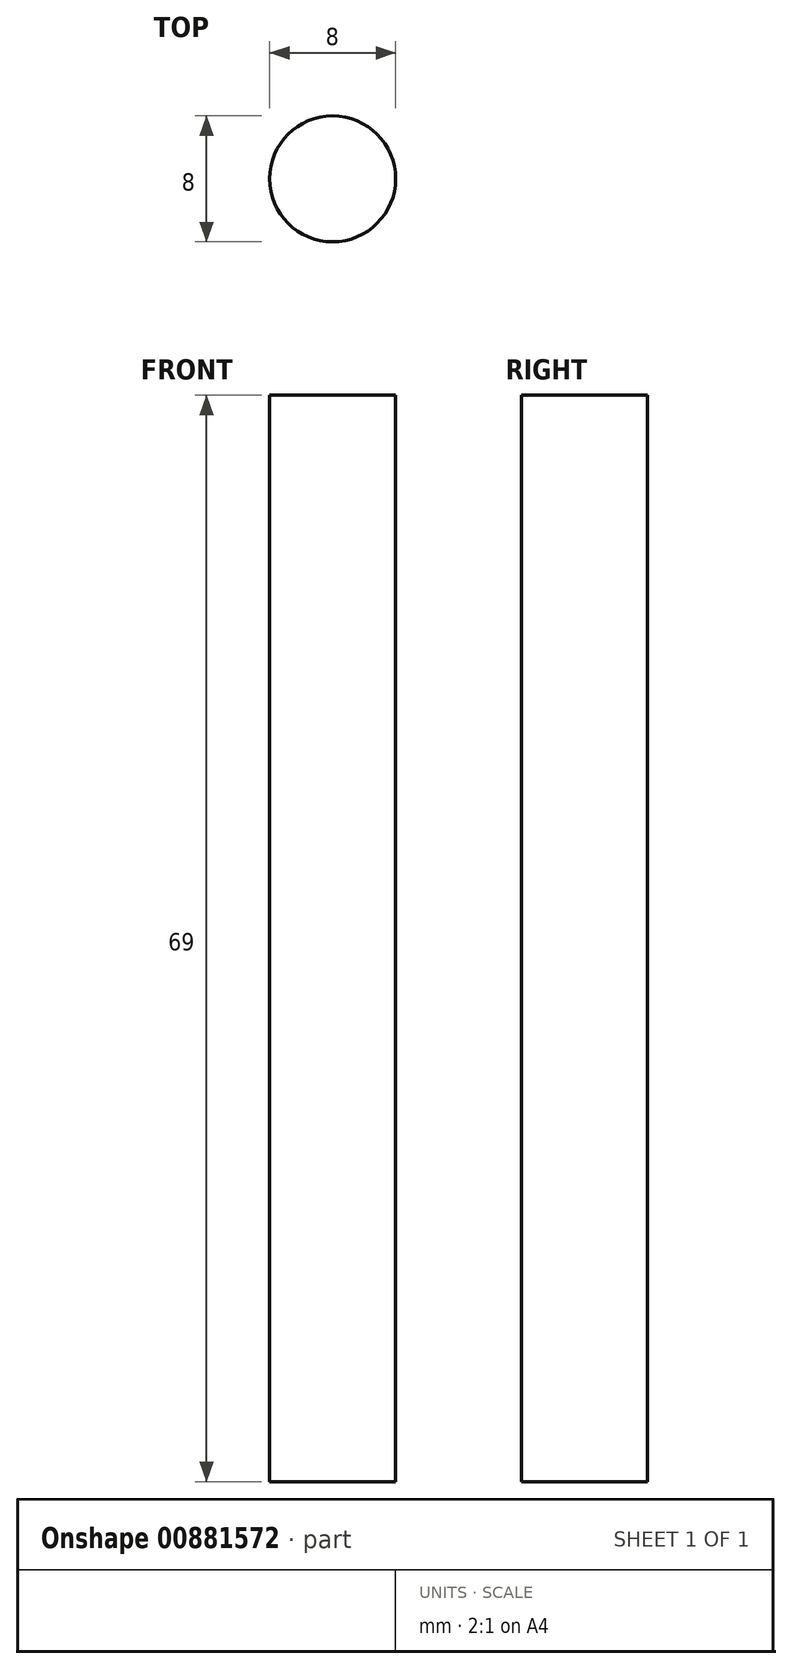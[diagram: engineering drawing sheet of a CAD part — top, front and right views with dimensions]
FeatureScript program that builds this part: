
annotation { "Feature Type Name" : "Feature", "Feature Type Description" : "" }
export const myFeature = defineFeature(function(context is Context, id is Id, definition is map)
    precondition{}
    {
        {
            var Q0;
            Q0=qCreatedBy(makeId("Top.planeOp"),FACE);
            var sketch = newSketch(context, id + "F0", { "sketchPlane" : qUnion([Q0])});
            skCircle(sketch, "E0", {"center": v(0, 0) * mm, "radius": 4 * mm});
            skSolve(sketch);
        }
        {
            var Q0;
            Q0 = qSketchRegion(id + "F0", true);
            extrude(context, id + "F1", {"entities" : qUnion([Q0]), "depth" : 69 * mm, "offsetDistance" : 25 * mm});
        }
    });
